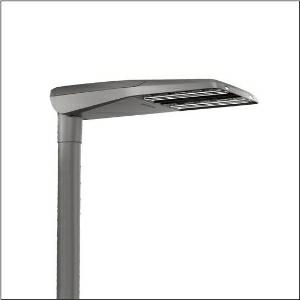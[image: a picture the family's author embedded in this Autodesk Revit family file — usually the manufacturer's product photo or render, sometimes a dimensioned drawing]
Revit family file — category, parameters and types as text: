
# Revit family: streetlight_sl_11_iq_midi___st1_2a_5xc3a21f08me_5047
name_source: partatom
category: Lighting Fixtures
units: mm (PartAtom-declared; Revit-internal decimal feet)

## family parameters
Cut with Voids When Loaded = No
Host = Face
Light Source = No
Part Type = Normal
Room Calculation Point = No
Round Connector Dimension = Use Diameter
Shared = No

## types (1)
- --- (1 x LED, 14840 lm, 124.7 W, 2200K)
    Apparent Load = 125 VA
    CIE Flux Codes = 32 70 96 100 100
    Color Rendering = 70
    Color Temperature = 2200K
    Default Elevation = 1800 mm
    Description = Streetlight SL 11 iQ midi, mast luminaire, primary light control with 3 zone facetted reflector, of plastic, silver coated, highly specular, primary optical cover: cover, of PMMA, transparent, light distribution: ST1.2a, light emission: direct distribution, primary light characteristic: asymmetric, installation type: post-top, side-entry, LED, High Power LED, rated luminous flux: 14.990lm, luminous efficacy: 120lm/W, light colour: 722, colour temperature: 2200K, control: Street-Remote, optimised constant luminous flux control (CLO 2.0), Desk-Remote (wireless, voltage-free reading and setting of iQ features in the workshop via application-optimized NFC function/RFID function), Light-Fading, Smart-Wire, Night-Set, Lumen-Switch, Temp-Guard, Auto-Match, with cable H07RN-F 5x 1.5mm², mains connection: 220..240V, AC, 50/60Hz, connection cable pre-assembled, cable length: 12,5m, start of lifetime: 125W, end of lifetime: 132W, reduction: 57W, luminaire housing, of diecast aluminium, powder-coated, Siteco® metallic grey (DB 702S), length: 780mm, width: 376mm, height: 118mm, spigot size: 60/76mm (post-top) and 42/60/76mm (side-entry), mast flange for spigot size: 42mm: 5XC10008XM4, 60mm: 5XC10008XM2, 76/60mm: 5XC10108XM1, equipment: Power, protection rating (complete): IP66, insulation class (complete): insulation class II (safety insulation), certification: CE, ENEC, VDE, impact resistance: IK09, permissible operating ambient temperature for outdoor applications: -25..+50°C, standard-compliant lighting for roads and squares, packaging unit: 1 piece

Light Distribution: ST1.2a
    Height = 118 mm
    Lamp = 1 x LED
    Lamp Light Flux = 14840 lm
    Lamp Power = 124.7 W
    Lamp count = 1
    Length = 780 mm
    Luminous efficacy = 119 lm/W
    Manufacturer = Siteco
    ModVariant = No
    Model = 5XC3A21F08ME
    Number of Poles = 1
    OnlyDefault = Yes
    Power Factor = 1
    Product Name = Streetlight SL 11 iQ midi | ST1.2a
    Product group = mast luminaire | pylon top
    ProductGroupID = 6100
    Protection Class = Protection class II
    Protection Degree = IP 66
    RLX_Detail_Level = 1
    RlxData = <blob elided: 70461 chars, md5=06a8e796>
    Socket = socket
    Standby Power = 0 W
    System Light Flux = 14841 lm
    System Power = 125 W
    Type Comments = factory setting: luminous flux: 100 % | dim-lin: 254 | 557 mA
    Type Image = l_1005960.jpg
    URL = http://relux.com
    VarID = @adj_039823
    Voltage = 0 V
    Weight = 0.00 kg
    Width = 376 mm

## geometry (parser evidence)
native form markers: Blend x4, Sweep x9
no freeform markers — native parametric forms only
